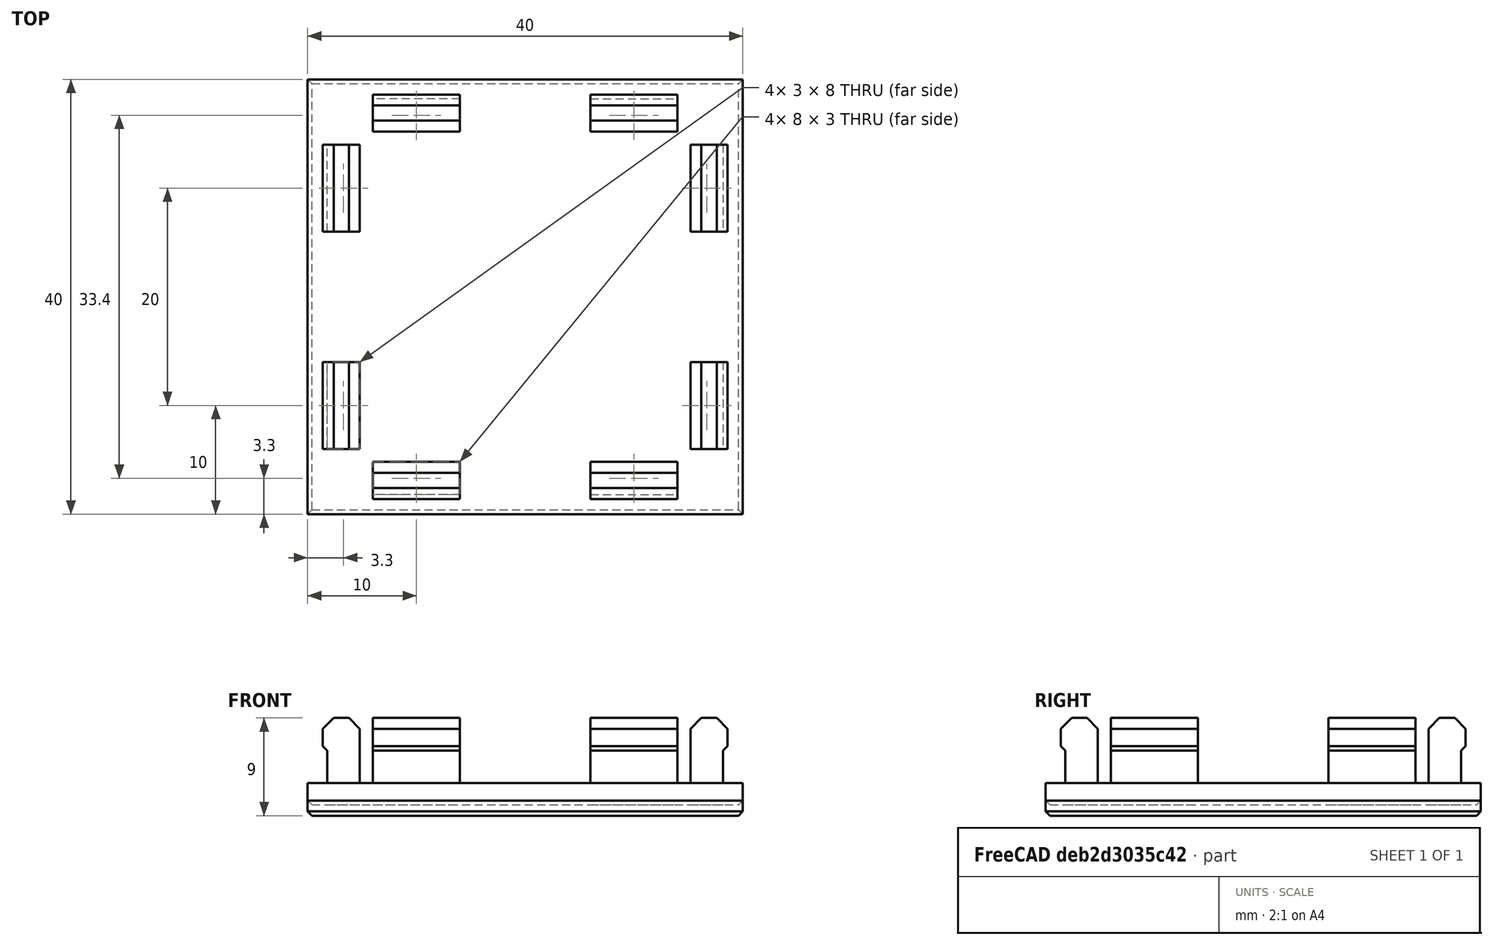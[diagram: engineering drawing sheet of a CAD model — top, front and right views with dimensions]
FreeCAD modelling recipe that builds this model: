
FCSTD DOCUMENT  (FreeCAD 0.18R14555 (Git shallow))
Label: table-foot
License: All rights reserved
LicenseURL: http://en.wikipedia.org/wiki/All_rights_reserved
objects: Part::Chamfer×8, Part::Box×7, Part::Feature×6, Part::MultiFuse×4
note: 25 computed .brp shape members not serialized (recipe doc carries the construction recipe); baked Part::Feature solids carry a one-line shape summary decoded from their .brp

FEATURE [Part::Box] Box  label="Cube"
  AttacherType = Attacher::AttachEngine3D
  Height = 3
  Length = 40
  Placement = pos=(-10,-10,-1) rot=(0,0,1;0rad)
  Width = 40
FEATURE [Part::Box] Box001  label="Cube001"
  AttacherType = Attacher::AttachEngine3D
  Height = 5
  Length = 8
  Placement = pos=(-4,5.2,0) rot=(0,0,1;0rad)
  Width = 3
FEATURE [Part::Box] Box002  label="Cube002"
  AttacherType = Attacher::AttachEngine3D
  Height = 5
  Length = 8
  Placement = pos=(-4,-8.2,0) rot=(0,0,1;0rad)
  Width = 3
FEATURE [Part::Box] Box011  label="Cube011"
  AttacherType = Attacher::AttachEngine3D
  Height = 3
  Length = 8
  Placement = pos=(-4,5.2,5) rot=(0,0,1;0rad)
  Width = 3.4
FEATURE [Part::Box] Box012  label="Cube012"
  AttacherType = Attacher::AttachEngine3D
  Height = 3
  Length = 8
  Placement = pos=(-4,-8.6,5) rot=(0,0,1;0rad)
  Width = 3.4
FEATURE [Part::Chamfer] Chamfer009002
  Base = -> Box012
  Edges = 1 edges r=0.4: [Edge9]
FEATURE [Part::Chamfer] Chamfer009003
  Base = -> Box011
  Edges = 1 edges r=0.4: [Edge11]
FEATURE [Part::Box] Box013  label="Cube013"
  AttacherType = Attacher::AttachEngine3D
  Height = 5
  Length = 3
  Placement = pos=(-8.2,-4,0) rot=(0,0,1;0rad)
  Width = 8
FEATURE [Part::Box] Box015  label="Cube015"
  AttacherType = Attacher::AttachEngine3D
  Height = 3
  Length = 3.4
  Placement = pos=(-8.6,-4,5) rot=(0,0,1;0rad)
  Width = 8
FEATURE [Part::Chamfer] Chamfer009007
  Base = -> Box015
  Edges = 1 edges r=0.4: [Edge4]
FEATURE [Part::Chamfer] Chamfer009009
  Base = -> Chamfer009007
  Edges = 2 edges r=1: [Edge3,Edge12]
FEATURE [Part::Chamfer] Chamfer009010
  Base = -> Chamfer009003
  Edges = 2 edges r=1: [Edge8,Edge12]
FEATURE [Part::Chamfer] Chamfer009012
  Base = -> Chamfer009002
  Edges = 2 edges r=1: [Edge8,Edge11]
FEATURE [Part::MultiFuse] Fusion
  Shapes = -> [Chamfer009009,Box013]
FEATURE [Part::MultiFuse] Fusion004
  Placement = pos=(0,20,0) rot=(0,0,1;0rad)
  Shapes = -> [Chamfer009010,Box001]
FEATURE [Part::MultiFuse] Fusion006
  Shapes = -> [Chamfer009012,Box002]
FEATURE [Part::Feature] Fusion006001  label="Fusion010"
  Placement = pos=(20,0,0) rot=(0,0,1;0rad)
  shape: bbox 8 x 3.4 x 8 mm, 13 faces (baked)
FEATURE [Part::Feature] Fusion004001  label="Fusion011"
  Placement = pos=(20,20,0) rot=(0,0,1;0rad)
  shape: bbox 8 x 3.4 x 8 mm, 13 faces (baked)
FEATURE [Part::Feature] Fusion005001  label="Fusion012"
  Placement = pos=(20,0,0) rot=(0,0,1;0rad)
  shape: bbox 3.4 x 8 x 8 mm, 13 faces (baked)
FEATURE [Part::Feature] Fusion006002  label="Fusion013"
  Placement = pos=(0,20,0) rot=(0,0,1;0rad)
  shape: bbox 3.4 x 8 x 8 mm, 13 faces (baked)
FEATURE [Part::Feature] Fusion005001001  label="Fusion014"
  Placement = pos=(20,20,0) rot=(0,0,1;0rad)
  shape: bbox 3.4 x 8 x 8 mm, 13 faces (baked)
FEATURE [Part::Feature] Fusion005001002001  label="2mm"
  shape: bbox 40 x 40 x 8 mm, 110 faces (baked)
FEATURE [Part::Chamfer] Chamfer  label="02-4040"
  Base = -> Fusion005001002001
  Edges = 4 edges r=0.4: [Edge4,Edge5,Edge42,Edge44]
FEATURE [Part::Chamfer] Chamfer009013
  Base = -> Box
  Edges = 4 edges r=0.4: [Edge4,Edge8,Edge9,Edge11]
FEATURE [Part::MultiFuse] Fusion005001002002  label="03-4040"
  Shapes = -> [Chamfer009013,Fusion005001,Fusion006001,Fusion004001,Fusion,Fusion006,Fusion004,Fusion005001001,Fusion006002]
